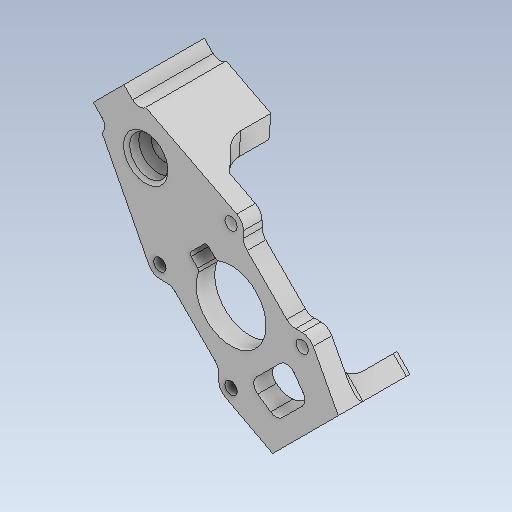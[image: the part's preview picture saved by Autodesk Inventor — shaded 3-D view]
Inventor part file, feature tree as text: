
AUTODESK INVENTOR PART (.ipt)
format: ipt  version: 2023 (Build 270158000, 158)  size: 510,976 bytes
history: native  units: mm
features: extrude x9, sketch x9, projected_geometry x9, fillet x7, thicken_offset x6, chamfer x5, other x5, reference x3, plane x2
ambient origin geometry x8: Origin, YZ Plane, XZ Plane, XY Plane, X Axis, Y Axis, Z Axis, Center Point
bodies: Solid1 (feature_tree)
feature tree (55):
  extrude  "Extrusion1"  Depth=32.0mm
  extrude  "Extrusion2"  Depth=15.0mm
  chamfer  "Chamfer1"  Distance=3.0mm
  extrude  "Extrusion3"  Depth=10.0mm TaperAngle=0.0deg
  chamfer  "Chamfer2"  Distance=2.0mm Angle=45.0deg
  fillet  "Fillet1"  Radius=19.5mm
  plane  "Work Plane1"
  plane  "Work Plane2"
  extrude  "Extrusion4"  Depth=10.0mm TaperAngle=0.0deg
  chamfer  "Chamfer3"  Distance=3.5mm Angle=45.0deg
  extrude  "Extrusion10"  [1 undecoded]
  extrude  "Extrusion11"  Depth=1.0mm
  fillet  "Fillet2"  Radius=10.0mm
  thicken_offset  "Thicken2"
  fillet  "Fillet3"  Radius=1.0mm
  fillet  "Fillet4"  Radius=8.0mm
  thicken_offset  "Thicken3"
  extrude  "Extrusion12"  Depth=2.0mm
  chamfer  "Chamfer7"  Distance=15.0mm
  fillet  "Fillet5"  Radius=10.0mm
  thicken_offset  "Thicken4"
  thicken_offset  "Thicken5"
  thicken_offset  "Thicken6"
  extrude  "Extrusion13"  Depth=4.0mm
  fillet  "Fillet8"  Radius=4.0mm
  extrude  "Extrusion14"  Depth=2.0mm TaperAngle=0.0deg
  fillet  "Fillet9"  Radius=1.5mm
  thicken_offset  "Thicken7"
  chamfer  "Chamfer10"  Distance=1.0mm
  sketch  "Sketch1"  dims[d0=6.0mm d1=32.0mm]
  reference  "Reference1"
  sketch  "Sketch2"  dims[d2=19.5mm d3=15.0mm]
  projected_geometry  "Projected Loop1"
  reference  "Reference2"
  sketch  "Sketch3"  dims[d4=15.0mm]
  projected_geometry  "Projected Loop2"
  sketch  "Sketch4"  dims[d5=10.0mm]
  projected_geometry  "Projected Loop3"
  sketch  "Sketch10"  dims[d6=10.0mm d7=3.0mm d8=0.0mm]
  projected_geometry  "Projected Loop9"
  reference  "Reference3"
  sketch  "Sketch11"  dims[d9=30.0mm d10=10.0mm d11=0.0mm d12=5.0mm d13=2.0mm d14=45.0deg d15=19.5mm]
  projected_geometry  "Projected Loop10"
  projected_geometry  "Projected Loop11"
  sketch  "Sketch12"  dims[d16=6.15mm d17=10.0mm d18=0.0mm d19=3.5mm d20=2.0mm d21=45.0deg]
  projected_geometry  "Projected Loop12"
  sketch  "Sketch13"  dims[d22=4.0mm d23=-2.0mm]
  projected_geometry  "Projected Loop13"
  sketch  "Sketch14"  dims[d24=-2.0mm d25=1.0mm d26=10.0mm d27=0.0mm d28=1.0mm d29=2.0mm d30=45.0deg d72=8.0mm d73=3.0mm d74=15.0mm d75=10.0mm d76=0.0mm d77=4.0mm d78=4.0mm d79=3.0mm d80=0.0mm d81=1.5mm d82=1.0mm d83=1.0mm d84=3.0mm d85=1.0mm d86=3.0mm d87=2.0mm d88=4.5mm d89=4.0mm d90=3.2mm d91=4.0mm d92=3.2mm d93=3.0mm d94=0.0mm d95=2.0mm d96=2.0mm d97=45.0deg d98=2.0mm d99=0.7mm d100=0.7mm d101=0.7mm d102=0.7mm d103=0.5mm d104=0.5mm d110=4.0mm d111=4.0mm d112=3.0mm d113=0.0mm d114=0.5mm d115=3.0mm d116=3.2mm d117=3.0mm d118=3.2mm d119=3.5mm d120=7.0mm d121=13.0mm d122=3.5mm d123=0.0mm d124=1.5mm d128=0.025mm d129=0.025mm d130=0.5mm d131=2.0mm d132=45.0deg d58=0.5mm d59=0.872665mm d60=0.5mm d61=0.872665mm]
  projected_geometry  "Projected Loop14"
  parser-record x1  (decoder bookkeeping rows leaked as tree rows — omitted from the tree; the rows remain in map.json)
  other  "reducer_1.iam"
  other  "mot_27_ass:1"
  other  "mot_27_2:1"
  other  "mot_27_1:1"
note: 1 required parameter value undecoded (feature->parameter linkage not recoverable at this tier; creation-order binding heuristic only, values carry confidence <= 0.55)
note: 1 file-system path scrubbed to <path> (originals preserved in map.json)
